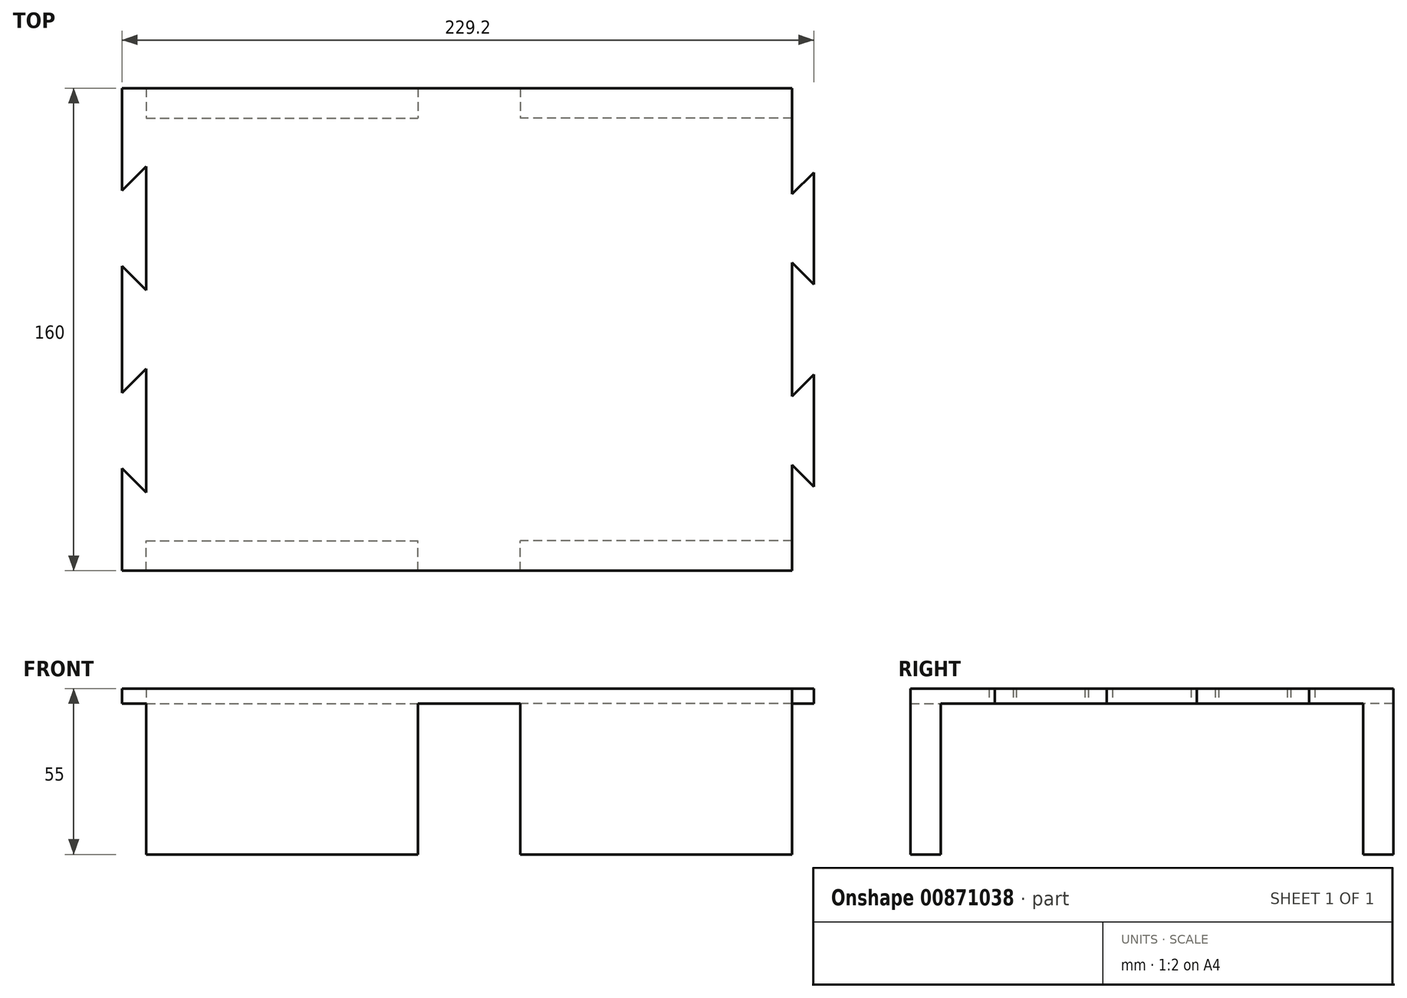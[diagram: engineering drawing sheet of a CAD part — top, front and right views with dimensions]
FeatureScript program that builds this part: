
annotation { "Feature Type Name" : "Feature", "Feature Type Description" : "" }
export const myFeature = defineFeature(function(context is Context, id is Id, definition is map)
    precondition{}
    {
        {
            var Q0;
            Q0=qCreatedBy(makeId("Top.planeOp"),FACE);
            var sketch = newSketch(context, id + "F0", { "sketchPlane" : qUnion([Q0])});
            skLineSegment(sketch, "E0.bottom", {"start": v(97.12, 75.18) * mm, "end": v(-124.88, 75.18) * mm});
            skLineSegment(sketch, "E0.top", {"start": v(97.12, -84.82) * mm, "end": v(-124.88, -84.82) * mm});
            skLineSegment(sketch, "E0.left", {"start": v(97.12, 75.18) * mm, "end": v(97.12, 40.05) * mm});
            skLineSegment(sketch, "E0.right", {"start": v(-124.88, 75.18) * mm, "end": v(-124.88, 41.18) * mm});
            skLineSegment(sketch, "E1", {"start": v(-124.88, 41.18) * mm, "end": v(-116.88, 49.18) * mm});
            skLineSegment(sketch, "E2", {"start": v(-116.88, 49.18) * mm, "end": v(-116.88, 8.18) * mm});
            skLineSegment(sketch, "E3", {"start": v(-116.88, 8.18) * mm, "end": v(-124.88, 16.18) * mm});
            skLineSegment(sketch, "E4", {"start": v(-124.88, -25.82) * mm, "end": v(-116.88, -17.82) * mm});
            skLineSegment(sketch, "E5", {"start": v(-116.88, -17.82) * mm, "end": v(-116.88, -58.82) * mm});
            skLineSegment(sketch, "E6", {"start": v(-116.88, -58.82) * mm, "end": v(-124.88, -50.82) * mm});
            skLineSegment(sketch, "E7", {"start": v(-116.88, 49.18) * mm, "end": v(-116.88, 75.18) * mm, "construction": true});
            skLineSegment(sketch, "E8", {"start": v(-116.88, 8.18) * mm, "end": v(-116.88, -17.82) * mm, "construction": true});
            skLineSegment(sketch, "E9", {"start": v(-116.88, -58.82) * mm, "end": v(-116.88, -84.82) * mm, "construction": true});
            skLineSegment(sketch, "E10.trimOffspring", {"start": v(-124.88, 16.18) * mm, "end": v(-124.88, -25.82) * mm});
            skLineSegment(sketch, "E11.trimOffspring", {"start": v(-124.88, -50.82) * mm, "end": v(-124.88, -84.82) * mm});
            skLineSegment(sketch, "E12.1.0.0", {"start": v(97.12, 41.18) * mm, "end": v(105.12, 49.18) * mm, "construction": true});
            skLineSegment(sketch, "E12.1.0.1", {"start": v(105.12, 49.18) * mm, "end": v(105.12, 8.18) * mm, "construction": true});
            skLineSegment(sketch, "E12.1.0.2", {"start": v(105.12, 8.18) * mm, "end": v(97.12, 16.18) * mm, "construction": true});
            skLineSegment(sketch, "E12.1.0.3", {"start": v(97.12, -25.82) * mm, "end": v(105.12, -17.82) * mm, "construction": true});
            skLineSegment(sketch, "E12.1.0.4", {"start": v(105.12, -17.82) * mm, "end": v(105.12, -58.82) * mm, "construction": true});
            skLineSegment(sketch, "E12.1.0.5", {"start": v(105.12, -58.82) * mm, "end": v(97.12, -50.82) * mm, "construction": true});
            skLineSegment(sketch, "E12.direction1", {"start": v(-124.88, 41.18) * mm, "end": v(97.12, 41.18) * mm, "construction": true});
            skLineSegment(sketch, "E13.0", {"start": v(104.32, 10.11) * mm, "end": v(97.12, 17.31) * mm});
            skLineSegment(sketch, "E13.1", {"start": v(104.32, 47.25) * mm, "end": v(104.32, 10.11) * mm});
            skLineSegment(sketch, "E13.2", {"start": v(97.12, 40.05) * mm, "end": v(104.32, 47.25) * mm});
            skLineSegment(sketch, "E14.0", {"start": v(104.32, -56.89) * mm, "end": v(97.12, -49.69) * mm});
            skLineSegment(sketch, "E14.1", {"start": v(104.32, -19.75) * mm, "end": v(104.32, -56.89) * mm});
            skLineSegment(sketch, "E14.2", {"start": v(97.12, -26.95) * mm, "end": v(104.32, -19.75) * mm});
            skLineSegment(sketch, "E15.bottom", {"start": v(-116.88, 75.18) * mm, "end": v(-26.88, 75.18) * mm});
            skLineSegment(sketch, "E15.top", {"start": v(-116.88, 65.18) * mm, "end": v(-26.88, 65.18) * mm});
            skLineSegment(sketch, "E15.left", {"start": v(-116.88, 75.18) * mm, "end": v(-116.88, 65.18) * mm});
            skLineSegment(sketch, "E15.right", {"start": v(-26.88, 75.18) * mm, "end": v(-26.88, 65.18) * mm});
            skLineSegment(sketch, "E16.bottom", {"start": v(97.12, 75.18) * mm, "end": v(7.12, 75.18) * mm});
            skLineSegment(sketch, "E16.top", {"start": v(97.12, 65.18) * mm, "end": v(7.12, 65.18) * mm});
            skLineSegment(sketch, "E16.left", {"start": v(97.12, 75.18) * mm, "end": v(97.12, 65.18) * mm});
            skLineSegment(sketch, "E16.right", {"start": v(7.12, 75.18) * mm, "end": v(7.12, 65.18) * mm});
            skLineSegment(sketch, "E17.bottom", {"start": v(-116.88, -84.82) * mm, "end": v(-26.88, -84.82) * mm});
            skLineSegment(sketch, "E17.top", {"start": v(-116.88, -74.82) * mm, "end": v(-26.88, -74.82) * mm});
            skLineSegment(sketch, "E17.left", {"start": v(-116.88, -84.82) * mm, "end": v(-116.88, -74.82) * mm});
            skLineSegment(sketch, "E17.right", {"start": v(-26.88, -84.82) * mm, "end": v(-26.88, -74.82) * mm});
            skLineSegment(sketch, "E18.bottom", {"start": v(97.12, -84.82) * mm, "end": v(7.12, -84.82) * mm});
            skLineSegment(sketch, "E18.top", {"start": v(97.12, -74.82) * mm, "end": v(7.12, -74.82) * mm});
            skLineSegment(sketch, "E18.left", {"start": v(97.12, -84.82) * mm, "end": v(97.12, -74.82) * mm});
            skLineSegment(sketch, "E18.right", {"start": v(7.12, -84.82) * mm, "end": v(7.12, -74.82) * mm});
            skLineSegment(sketch, "E19.trimOffspring", {"start": v(97.12, 17.31) * mm, "end": v(97.12, -26.95) * mm});
            skLineSegment(sketch, "E20.trimOffspring", {"start": v(97.12, -49.69) * mm, "end": v(97.12, -84.82) * mm});
            skSolve(sketch);
        }
        {
            var Q0;
            {var subQ6=sQuery(id+"F0.wireOp",EDGE,"E0.right");Q0=makeQuery(id+"F0.imprint","IMPRINT",FACE,{"disambiguationData":[TD([[makeQuery(id+"F0.imprint","IMPRINT",EDGE,{"derivedFrom":subQ6}),1.0]])]});}
            var Q1;
            Q1=makeQuery(id+"F0.imprint","IMPRINT",FACE,{"disambiguationData":[TD([[makeQuery(id+"F0.imprint","IMPRINT",EDGE,{"derivedFrom":sQuery(id+"F0.wireOp",EDGE,"E15.top")}),1.0]])]});
            var Q2;
            {var subQ4=sQuery(id+"F0.wireOp",EDGE,"E16.top");Q2=makeQuery(id+"F0.imprint","IMPRINT",FACE,{"disambiguationData":[TD([[makeQuery(id+"F0.imprint","IMPRINT",EDGE,{"derivedFrom":subQ4}),-1.0]])]});}
            var Q3;
            Q3=makeQuery(id+"F0.imprint","IMPRINT",FACE,{"disambiguationData":[TD([[makeQuery(id+"F0.imprint","IMPRINT",EDGE,{"derivedFrom":sQuery(id+"F0.wireOp",EDGE,"E18.top")}),1.0]])]});
            var Q4;
            Q4=makeQuery(id+"F0.imprint","IMPRINT",FACE,{"disambiguationData":[TD([[makeQuery(id+"F0.imprint","IMPRINT",EDGE,{"derivedFrom":sQuery(id+"F0.wireOp",EDGE,"E17.top")}),-1.0]])]});
            extrude(context, id + "F1", {"entities" : qUnion([Q0, Q1, Q2, Q3, Q4]), "depth" : 5 * mm, "offsetDistance" : 25 * mm});
        }
        {
            var Q0;
            {var subQ4=sQuery(id+"F0.wireOp",EDGE,"E16.top");Q0=makeQuery(id+"F0.imprint","IMPRINT",FACE,{"disambiguationData":[TD([[makeQuery(id+"F0.imprint","IMPRINT",EDGE,{"derivedFrom":subQ4}),-1.0]])]});}
            var Q1;
            Q1=makeQuery(id+"F0.imprint","IMPRINT",FACE,{"disambiguationData":[TD([[makeQuery(id+"F0.imprint","IMPRINT",EDGE,{"derivedFrom":sQuery(id+"F0.wireOp",EDGE,"E15.top")}),1.0]])]});
            var Q2;
            Q2=makeQuery(id+"F0.imprint","IMPRINT",FACE,{"disambiguationData":[TD([[makeQuery(id+"F0.imprint","IMPRINT",EDGE,{"derivedFrom":sQuery(id+"F0.wireOp",EDGE,"E17.top")}),-1.0]])]});
            var Q3;
            Q3=makeQuery(id+"F0.imprint","IMPRINT",FACE,{"disambiguationData":[TD([[makeQuery(id+"F0.imprint","IMPRINT",EDGE,{"derivedFrom":sQuery(id+"F0.wireOp",EDGE,"E18.top")}),1.0]])]});
            extrude(context, id + "F2", {"entities" : qUnion([Q0, Q1, Q2, Q3]), "operationType" : NewBodyOperationType.ADD, "oppositeDirection" : true, "depth" : 50 * mm, "offsetDistance" : 25 * mm});
        }
    });
